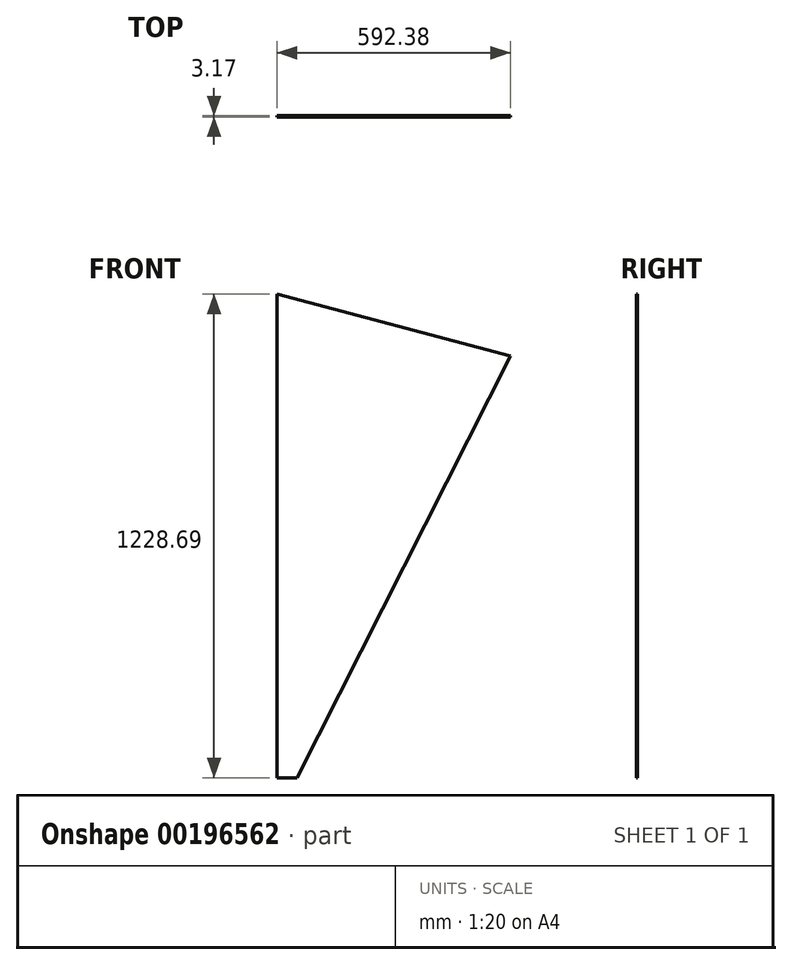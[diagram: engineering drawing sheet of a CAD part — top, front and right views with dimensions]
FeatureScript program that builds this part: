
annotation { "Feature Type Name" : "Feature", "Feature Type Description" : "" }
export const myFeature = defineFeature(function(context is Context, id is Id, definition is map)
    precondition{}
    {
        {
            var Q0;
            Q0=qCreatedBy(makeId("Front.planeOp"),FACE);
            var sketch = newSketch(context, id + "F0", { "sketchPlane" : qUnion([Q0])});
            skLineSegment(sketch, "E0", {"start": v(133.72, -459.92) * mm, "end": v(133.72, 768.77) * mm});
            skLineSegment(sketch, "E1.MirrorCS", {"start": v(133.72, 768.77) * mm, "end": v(726.1, 611) * mm});
            skLineSegment(sketch, "E2.MirrorCS", {"start": v(726.1, 611) * mm, "end": v(184.52, -459.92) * mm});
            skLineSegment(sketch, "E3.MirrorCS", {"start": v(133.72, -459.92) * mm, "end": v(184.52, -459.92) * mm});
            skSolve(sketch);
        }
        {
            var Q0;
            Q0=makeQuery(id+"F0.imprint","IMPRINT",FACE,{"disambiguationData":[TD([[makeQuery(id+"F0.imprint","IMPRINT",EDGE,{"derivedFrom":sQuery(id+"F0.wireOp",EDGE,"E0")}),-1.0]])]});
            extrude(context, id + "F1", {"entities" : qUnion([Q0]), "depth" : 3.17 * mm});
        }
    });
